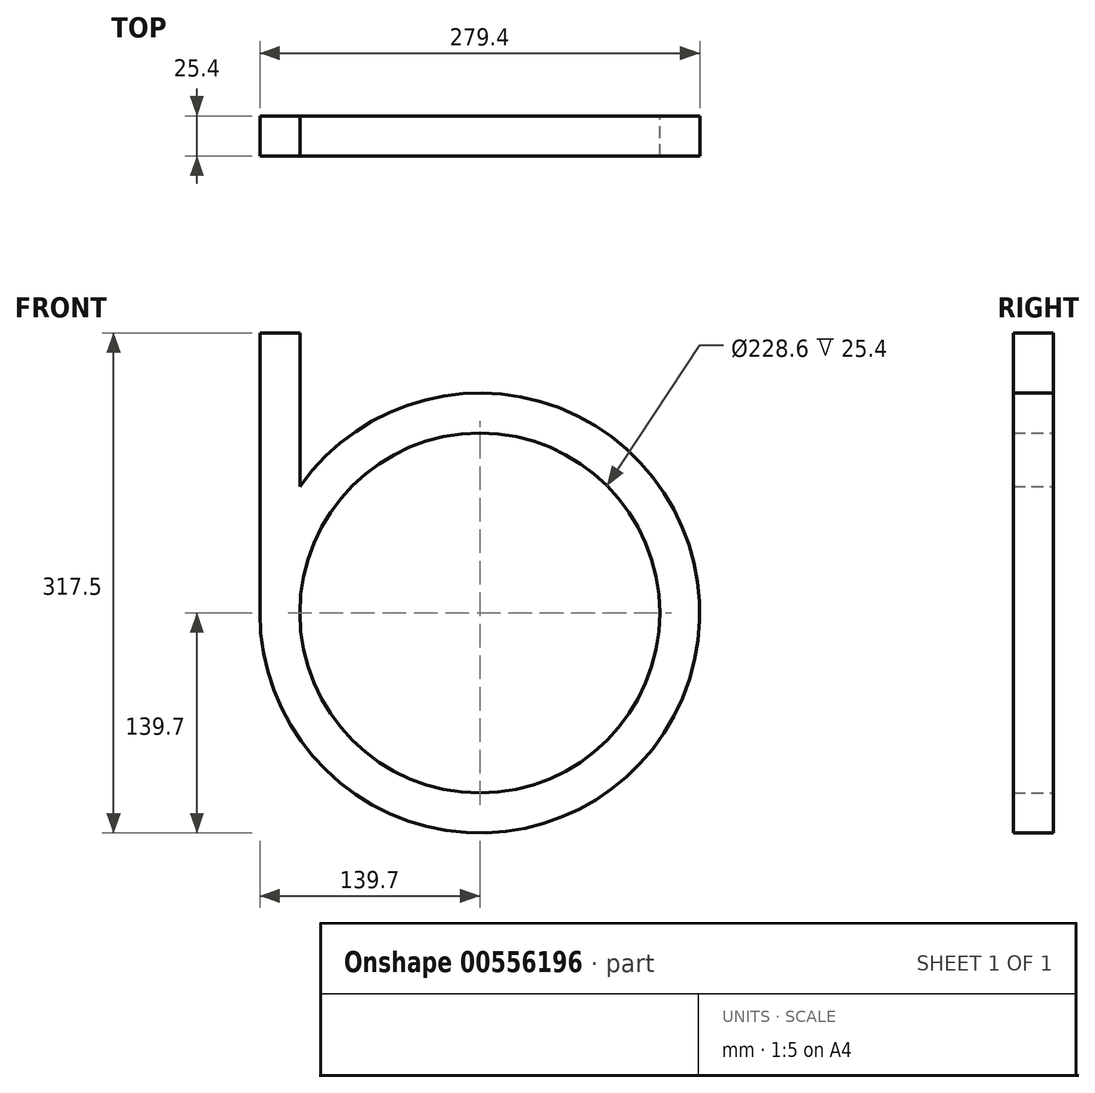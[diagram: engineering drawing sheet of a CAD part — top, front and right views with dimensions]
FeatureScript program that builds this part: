
annotation { "Feature Type Name" : "Feature", "Feature Type Description" : "" }
export const myFeature = defineFeature(function(context is Context, id is Id, definition is map)
    precondition{}
    {
        {
            var Q0;
            Q0=qCreatedBy(makeId("Front.planeOp"),FACE);
            var sketch = newSketch(context, id + "F0", { "sketchPlane" : qUnion([Q0])});
            skArc(sketch, "E0", {"start": v(-139.7, 0) * mm, "mid": v(133.2, -42.12) * mm, "end": v(-114.3, 80.32) * mm});
            skCircle(sketch, "E1", {"center": v(0, 0) * mm, "radius": 114.3 * mm});
            skLineSegment(sketch, "E2", {"start": v(-139.7, 0) * mm, "end": v(-139.7, 177.8) * mm});
            skLineSegment(sketch, "E3", {"start": v(-139.7, 177.8) * mm, "end": v(-114.3, 177.8) * mm});
            skLineSegment(sketch, "E4", {"start": v(-114.3, 177.8) * mm, "end": v(-114.3, 80.32) * mm});
            skSolve(sketch);
        }
        {
            var Q0;
            Q0 = qSketchRegion(id + "F0", true);
            extrude(context, id + "F1", {"entities" : qUnion([Q0]), "depth" : 25.4 * mm, "offsetDistance" : 25.4 * mm});
        }
    });
